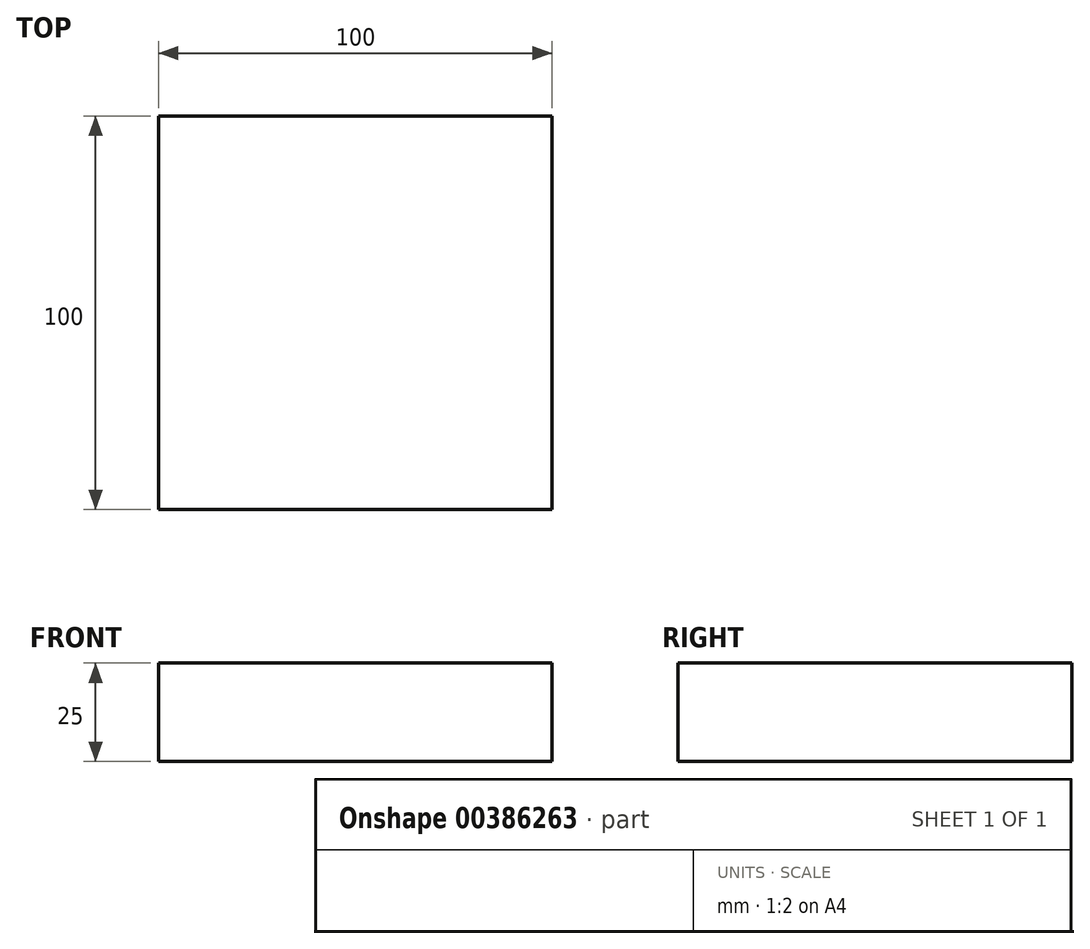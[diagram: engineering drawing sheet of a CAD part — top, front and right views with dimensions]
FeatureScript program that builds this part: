
annotation { "Feature Type Name" : "Feature", "Feature Type Description" : "" }
export const myFeature = defineFeature(function(context is Context, id is Id, definition is map)
    precondition{}
    {
        {
            var Q0;
            Q0=qCreatedBy(makeId("Top.planeOp"),FACE);
            var sketch = newSketch(context, id + "F0", { "sketchPlane" : qUnion([Q0])});
            skLineSegment(sketch, "E0.bottom", {"start": v(-50, -50) * mm, "end": v(50, -50) * mm});
            skLineSegment(sketch, "E0.top", {"start": v(-50, 50) * mm, "end": v(50, 50) * mm});
            skLineSegment(sketch, "E0.left", {"start": v(-50, -50) * mm, "end": v(-50, 50) * mm});
            skLineSegment(sketch, "E0.right", {"start": v(50, -50) * mm, "end": v(50, 50) * mm});
            skPoint(sketch, "E0.middle", {"position": v(0, 0) * mm});
            skSolve(sketch);
        }
        {
            var Q0;
            Q0=makeQuery(id+"F0.imprint","IMPRINT",FACE,{"disambiguationData":[TD([[makeQuery(id+"F0.imprint","IMPRINT",EDGE,{"derivedFrom":sQuery(id+"F0.wireOp",EDGE,"E0.bottom")}),1.0]])]});
            extrude(context, id + "F1", {"entities" : qUnion([Q0]), "depth" : 25 * mm});
        }
    });
